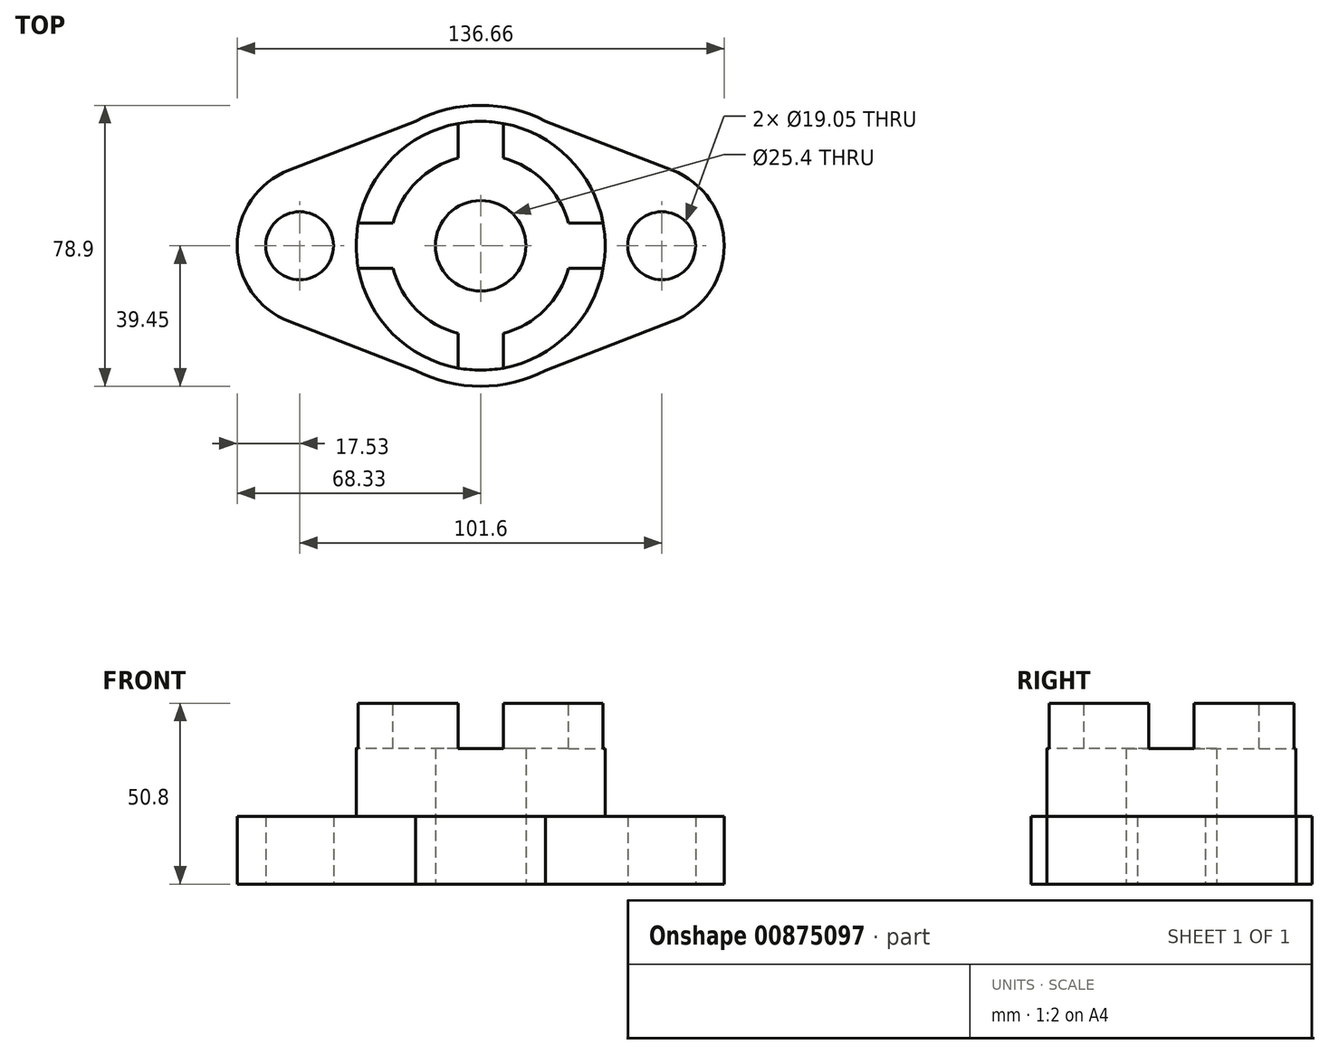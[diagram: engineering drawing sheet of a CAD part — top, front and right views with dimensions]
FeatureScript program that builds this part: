
annotation { "Feature Type Name" : "Feature", "Feature Type Description" : "" }
export const myFeature = defineFeature(function(context is Context, id is Id, definition is map)
    precondition{}
    {
        {
            var Q0;
            Q0=qCreatedBy(makeId("Top.planeOp"),FACE);
            var sketch = newSketch(context, id + "F0", { "sketchPlane" : qUnion([Q0])});
            skPoint(sketch, "E0.middle", {"position": v(0, 0) * mm});
            skCircle(sketch, "E1", {"center": v(0, 0) * mm, "radius": 34.93 * mm});
            skCircle(sketch, "E2", {"center": v(0, 0) * mm, "radius": 25.4 * mm});
            skCircle(sketch, "E3", {"center": v(0, 0) * mm, "radius": 12.7 * mm});
            skLineSegment(sketch, "E4", {"start": v(0, 0) * mm, "end": v(50.8, 0) * mm});
            skLineSegment(sketch, "E5", {"start": v(0, 0) * mm, "end": v(-50.8, 0) * mm});
            skCircle(sketch, "E6", {"center": v(-50.8, 0) * mm, "radius": 9.53 * mm});
            skCircle(sketch, "E7", {"center": v(50.8, 0) * mm, "radius": 9.53 * mm});
            skPoint(sketch, "E0.top.end.orphan", {"position": v(-50.8, -50.8) * mm});
            skPoint(sketch, "E8.orphan", {"position": v(50.8, -50.8) * mm});
            skPoint(sketch, "E0.bottom.start.orphan", {"position": v(50.8, 50.8) * mm});
            skPoint(sketch, "E9.orphan", {"position": v(-50.8, 50.8) * mm});
            skPoint(sketch, "E10.trimOffspring.end.orphan", {"position": v(3.85, 36.21) * mm});
            skPoint(sketch, "E11.end.orphan", {"position": v(0, 36.21) * mm});
            skPoint(sketch, "E12.orphan", {"position": v(0, 40.33) * mm});
            skArc(sketch, "E13", {"start": v(18.23, 34.99) * mm, "mid": v(0, 39.45) * mm, "end": v(-18.23, 34.99) * mm});
            skArc(sketch, "E14", {"start": v(-53.77, 21.24) * mm, "mid": v(-68.33, 0) * mm, "end": v(-53.77, -21.24) * mm});
            skArc(sketch, "E15", {"start": v(-18.23, -34.99) * mm, "mid": v(0, -39.45) * mm, "end": v(18.23, -34.99) * mm});
            skArc(sketch, "E16", {"start": v(53.77, -21.24) * mm, "mid": v(68.33, 0) * mm, "end": v(53.77, 21.24) * mm});
            skPoint(sketch, "E17.orphan", {"position": v(-68.33, 0) * mm});
            skPoint(sketch, "E18.orphan", {"position": v(0, -39.45) * mm});
            skPoint(sketch, "E19.orphan", {"position": v(68.33, 0) * mm});
            skPoint(sketch, "E20.start.orphan", {"position": v(0, 39.45) * mm});
            skLineSegment(sketch, "E21", {"start": v(-18.23, 34.99) * mm, "end": v(-53.77, 21.24) * mm});
            skPoint(sketch, "E22.orphan", {"position": v(-34.17, 19.73) * mm});
            skLineSegment(sketch, "E23", {"start": v(18.23, 34.99) * mm, "end": v(53.77, 21.24) * mm});
            skPoint(sketch, "E24.orphan", {"position": v(34.17, 19.73) * mm});
            skLineSegment(sketch, "E25", {"start": v(-18.23, -34.99) * mm, "end": v(-53.77, -21.24) * mm});
            skPoint(sketch, "E26.orphan", {"position": v(-34.17, -19.73) * mm});
            skLineSegment(sketch, "E27", {"start": v(18.23, -34.99) * mm, "end": v(53.77, -21.24) * mm});
            skPoint(sketch, "E28.orphan", {"position": v(34.17, -19.73) * mm});
            skSolve(sketch);
        }
        {
            var Q0;
            {var subQ1=sQuery(id+"F0.wireOp",EDGE,"E0.top");Q0=makeQuery(id+"F0.imprint","IMPRINT",FACE,{"disambiguationData":[TD([[makeQuery(id+"F0.imprint","IMPRINT",EDGE,{"derivedFrom":subQ1}),-1.0]])]});}
            var Q1;
            {var subQ1=sQuery(id+"F0.wireOp",EDGE,"E0.bottom");Q1=makeQuery(id+"F0.imprint","IMPRINT",FACE,{"disambiguationData":[TD([[makeQuery(id+"F0.imprint","IMPRINT",EDGE,{"derivedFrom":subQ1}),1.0]])]});}
            var Q2;
            {var subQ0=sQuery(id+"F0.wireOp",EDGE,"E4");var subQ1=sQuery(id+"F0.wireOp",EDGE,"E1");var subQ2=makeQuery(id+"F0.imprint","INTERSECT",VERTEX,{"derivedFrom":[subQ1,subQ0]});Q2=makeQuery(id+"F0.imprint","IMPRINT",FACE,{"disambiguationData":[TD([[makeQuery(id+"F0.imprint","IMPRINT",EDGE,{"disambiguationData":[TD([[subQ2,1.0]])],"derivedFrom":subQ1}),1.0]])]});}
            var Q3;
            {var subQ0=sQuery(id+"F0.wireOp",EDGE,"E4");var subQ1=sQuery(id+"F0.wireOp",EDGE,"E1");var subQ2=makeQuery(id+"F0.imprint","INTERSECT",VERTEX,{"derivedFrom":[subQ1,subQ0]});Q3=makeQuery(id+"F0.imprint","IMPRINT",FACE,{"disambiguationData":[TD([[makeQuery(id+"F0.imprint","IMPRINT",EDGE,{"disambiguationData":[TD([[subQ2,-1.0]])],"derivedFrom":subQ1}),1.0]])]});}
            extrude(context, id + "F1", {"entities" : qUnion([Q0, Q1, Q2, Q3]), "depth" : 19.05 * mm, "offsetDistance" : 25.4 * mm});
        }
        {
            var Q0;
            {var subQ0=sQuery(id+"F0.wireOp",EDGE,"E4");var subQ1=sQuery(id+"F0.wireOp",EDGE,"E1");var subQ2=makeQuery(id+"F0.imprint","INTERSECT",VERTEX,{"derivedFrom":[subQ1,subQ0]});Q0=makeQuery(id+"F0.imprint","IMPRINT",FACE,{"disambiguationData":[TD([[makeQuery(id+"F0.imprint","IMPRINT",EDGE,{"disambiguationData":[TD([[subQ2,1.0]])],"derivedFrom":subQ1}),1.0]])]});}
            var Q1;
            {var subQ0=sQuery(id+"F0.wireOp",EDGE,"E4");var subQ1=sQuery(id+"F0.wireOp",EDGE,"E1");var subQ2=makeQuery(id+"F0.imprint","INTERSECT",VERTEX,{"derivedFrom":[subQ1,subQ0]});Q1=makeQuery(id+"F0.imprint","IMPRINT",FACE,{"disambiguationData":[TD([[makeQuery(id+"F0.imprint","IMPRINT",EDGE,{"disambiguationData":[TD([[subQ2,-1.0]])],"derivedFrom":subQ1}),1.0]])]});}
            var Q2;
            {var subQ0=sQuery(id+"F0.wireOp",EDGE,"E4");var subQ1=sQuery(id+"F0.wireOp",EDGE,"E2");var subQ2=makeQuery(id+"F0.imprint","INTERSECT",VERTEX,{"derivedFrom":[subQ1,subQ0]});Q2=makeQuery(id+"F0.imprint","IMPRINT",FACE,{"disambiguationData":[TD([[makeQuery(id+"F0.imprint","IMPRINT",EDGE,{"disambiguationData":[TD([[subQ2,1.0]])],"derivedFrom":subQ1}),1.0]])]});}
            var Q3;
            {var subQ0=sQuery(id+"F0.wireOp",EDGE,"E4");var subQ1=sQuery(id+"F0.wireOp",EDGE,"E2");var subQ2=makeQuery(id+"F0.imprint","INTERSECT",VERTEX,{"derivedFrom":[subQ1,subQ0]});Q3=makeQuery(id+"F0.imprint","IMPRINT",FACE,{"disambiguationData":[TD([[makeQuery(id+"F0.imprint","IMPRINT",EDGE,{"disambiguationData":[TD([[subQ2,-1.0]])],"derivedFrom":subQ1}),1.0]])]});}
            extrude(context, id + "F2", {"entities" : qUnion([Q0, Q1, Q2, Q3]), "operationType" : NewBodyOperationType.ADD, "depth" : 38.1 * mm, "offsetDistance" : 25.4 * mm});
        }
        {
            var Q0;
            Q0=makeQuery(id+"F2.opExtrude","CAP_FACE",FACE,{"disambiguationData":[OSD([sQuery(id+"F0.wireOp",EDGE,"E1"),sQuery(id+"F0.wireOp",EDGE,"E3")])],"isStart":false});
            var sketch = newSketch(context, id + "F3", { "sketchPlane" : qUnion([Q0])});
            skCircle(sketch, "E29", {"center": v(0, 0) * mm, "radius": 34.93 * mm});
            skSolve(sketch);
        }
        {
            var Q0;
            Q0=makeQuery(id+"F3.imprint","IMPRINT",FACE,{"disambiguationData":[TD([[makeQuery(id+"F3.imprint","IMPRINT",EDGE,{"derivedFrom":sQuery(id+"F3.wireOp",EDGE,"E29")}),1.0]])]});
            extrude(context, id + "F4", {"entities" : qUnion([Q0]), "operationType" : NewBodyOperationType.ADD, "depth" : 12.7 * mm, "offsetDistance" : 25.4 * mm});
        }
        {
            var Q0;
            Q0=makeQuery(id+"F4.opExtrude","CAP_FACE",FACE,{"disambiguationData":[OSD([sQuery(id+"F0.wireOp",EDGE,"E3"),sQuery(id+"F3.wireOp",EDGE,"E29")])],"isStart":false});
            var sketch = newSketch(context, id + "F5", { "sketchPlane" : qUnion([Q0])});
            skLineSegment(sketch, "E30", {"start": v(0, 0) * mm, "end": v(6.35, 0) * mm});
            skLineSegment(sketch, "E31", {"start": v(0, 0) * mm, "end": v(-6.35, 0) * mm});
            skLineSegment(sketch, "E32", {"start": v(-6.35, 0) * mm, "end": v(-6.35, 34.34) * mm});
            skLineSegment(sketch, "E33", {"start": v(-6.35, 0) * mm, "end": v(-6.35, -34.34) * mm});
            skLineSegment(sketch, "E34", {"start": v(6.35, 0) * mm, "end": v(6.35, 34.34) * mm});
            skLineSegment(sketch, "E35", {"start": v(6.35, 0) * mm, "end": v(6.35, -34.34) * mm});
            skLineSegment(sketch, "E36", {"start": v(0, 0) * mm, "end": v(0, 6.35) * mm});
            skLineSegment(sketch, "E37", {"start": v(0, 6.35) * mm, "end": v(34.34, 6.35) * mm});
            skLineSegment(sketch, "E38", {"start": v(0, 6.35) * mm, "end": v(-34.34, 6.35) * mm});
            skLineSegment(sketch, "E39", {"start": v(0, 0) * mm, "end": v(0, -6.35) * mm});
            skLineSegment(sketch, "E40", {"start": v(0, -6.35) * mm, "end": v(-34.34, -6.35) * mm});
            skLineSegment(sketch, "E41", {"start": v(0, -6.35) * mm, "end": v(34.34, -6.35) * mm});
            skCircle(sketch, "E42", {"center": v(0, 0) * mm, "radius": 25.4 * mm});
            skSolve(sketch);
        }
        {
            var Q0;
            {var subQ0=sQuery(id+"F5.wireOp",EDGE,"E38");var subQ1=makeQuery(id+"F4.opExtrude","CAP_EDGE",EDGE,{"disambiguationData":[OSD([sQuery(id+"F3.wireOp",EDGE,"E29")])],"isStart":false});var subQ2=makeQuery(id+"F5.imprint","INTERSECT",VERTEX,{"derivedFrom":[subQ1,subQ0]});Q0=makeQuery(id+"F5.imprint","IMPRINT",FACE,{"disambiguationData":[TD([[makeQuery(id+"F5.imprint","IMPRINT",EDGE,{"disambiguationData":[TD([[subQ2,1.0]])],"derivedFrom":subQ0}),1.0]])]});}
            var Q1;
            {var subQ0=sQuery(id+"F5.wireOp",EDGE,"E33");var subQ1=makeQuery(id+"F4.opExtrude","CAP_EDGE",EDGE,{"disambiguationData":[OSD([sQuery(id+"F3.wireOp",EDGE,"E29")])],"isStart":false});var subQ2=makeQuery(id+"F5.imprint","INTERSECT",VERTEX,{"derivedFrom":[subQ1,subQ0]});Q1=makeQuery(id+"F5.imprint","IMPRINT",FACE,{"disambiguationData":[TD([[makeQuery(id+"F5.imprint","IMPRINT",EDGE,{"disambiguationData":[TD([[subQ2,1.0]])],"derivedFrom":subQ0}),1.0]])]});}
            var Q2;
            {var subQ0=sQuery(id+"F5.wireOp",EDGE,"E37");var subQ1=makeQuery(id+"F4.opExtrude","CAP_EDGE",EDGE,{"disambiguationData":[OSD([sQuery(id+"F3.wireOp",EDGE,"E29")])],"isStart":false});var subQ2=makeQuery(id+"F5.imprint","INTERSECT",VERTEX,{"derivedFrom":[subQ1,subQ0]});Q2=makeQuery(id+"F5.imprint","IMPRINT",FACE,{"disambiguationData":[TD([[makeQuery(id+"F5.imprint","IMPRINT",EDGE,{"disambiguationData":[TD([[subQ2,1.0]])],"derivedFrom":subQ0}),-1.0]])]});}
            var Q3;
            {var subQ0=sQuery(id+"F5.wireOp",EDGE,"E32");var subQ1=makeQuery(id+"F4.opExtrude","CAP_EDGE",EDGE,{"disambiguationData":[OSD([sQuery(id+"F3.wireOp",EDGE,"E29")])],"isStart":false});var subQ2=makeQuery(id+"F5.imprint","INTERSECT",VERTEX,{"derivedFrom":[subQ1,subQ0]});Q3=makeQuery(id+"F5.imprint","IMPRINT",FACE,{"disambiguationData":[TD([[makeQuery(id+"F5.imprint","IMPRINT",EDGE,{"disambiguationData":[TD([[subQ2,1.0]])],"derivedFrom":subQ0}),-1.0]])]});}
            extrude(context, id + "F6", {"entities" : qUnion([Q0, Q1, Q2, Q3]), "operationType" : NewBodyOperationType.REMOVE, "oppositeDirection" : true, "depth" : 12.7 * mm, "offsetDistance" : 25.4 * mm});
        }
        {
            var Q0;
            Q0=makeQuery(id+"F0.imprint","IMPRINT",FACE,{"disambiguationData":[TD([[makeQuery(id+"F0.imprint","IMPRINT",EDGE,{"derivedFrom":sQuery(id+"F0.wireOp",EDGE,"E6")}),-1.0]])]});
            extrude(context, id + "F7", {"entities" : qUnion([Q0]), "operationType" : NewBodyOperationType.ADD, "depth" : 19.05 * mm, "offsetDistance" : 25.4 * mm});
        }
        {
            var Q0;
            Q0 = qSketchRegion(id + "F5", true);
            extrude(context, id + "F8", {"entities" : qUnion([Q0]), "operationType" : NewBodyOperationType.REMOVE, "oppositeDirection" : true, "depth" : 103.38 * mm, "offsetDistance" : 25.4 * mm});
        }
        {
            var Q0;
            {var subQ0=sQuery(id+"F0.wireOp",EDGE,"E4");var subQ1=sQuery(id+"F0.wireOp",EDGE,"E2");var subQ2=makeQuery(id+"F0.imprint","INTERSECT",VERTEX,{"derivedFrom":[subQ1,subQ0]});Q0=makeQuery(id+"F0.imprint","IMPRINT",FACE,{"disambiguationData":[TD([[makeQuery(id+"F0.imprint","IMPRINT",EDGE,{"disambiguationData":[TD([[subQ2,1.0]])],"derivedFrom":subQ1}),1.0]])]});}
            var Q1;
            {var subQ0=sQuery(id+"F0.wireOp",EDGE,"E4");var subQ1=sQuery(id+"F0.wireOp",EDGE,"E2");var subQ2=makeQuery(id+"F0.imprint","INTERSECT",VERTEX,{"derivedFrom":[subQ1,subQ0]});Q1=makeQuery(id+"F0.imprint","IMPRINT",FACE,{"disambiguationData":[TD([[makeQuery(id+"F0.imprint","IMPRINT",EDGE,{"disambiguationData":[TD([[subQ2,-1.0]])],"derivedFrom":subQ1}),1.0]])]});}
            extrude(context, id + "F9", {"entities" : qUnion([Q0, Q1]), "operationType" : NewBodyOperationType.ADD, "depth" : 38.1 * mm, "offsetDistance" : 25.4 * mm});
        }
    });
